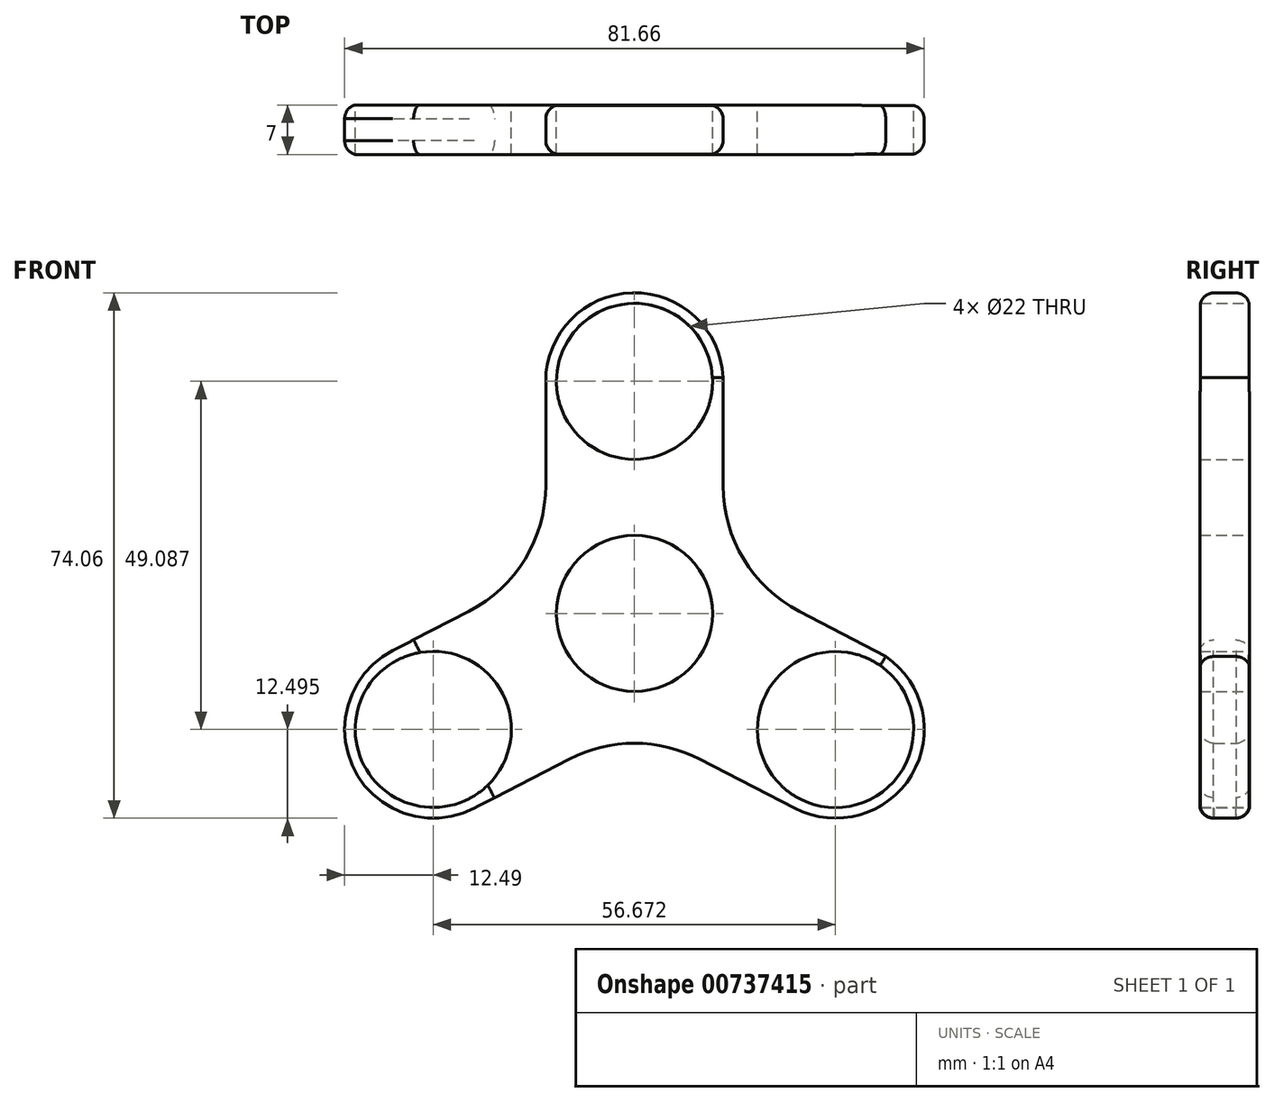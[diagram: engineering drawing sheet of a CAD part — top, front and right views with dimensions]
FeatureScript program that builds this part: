
annotation { "Feature Type Name" : "Feature", "Feature Type Description" : "" }
export const myFeature = defineFeature(function(context is Context, id is Id, definition is map)
    precondition{}
    {
        {
            var Q0;
            Q0=qCreatedBy(makeId("Front.planeOp"),FACE);
            var sketch = newSketch(context, id + "F0", { "sketchPlane" : qUnion([Q0])});
            skLineSegment(sketch, "E0", {"start": v(-27, 38.07) * mm, "end": v(-27, 0) * mm});
            skLineSegment(sketch, "E1", {"start": v(-27, 0) * mm, "end": v(-44.34, 0) * mm});
            skLineSegment(sketch, "E2", {"start": v(-44.34, 0) * mm, "end": v(-31.06, 17.05) * mm});
            skLineSegment(sketch, "E3", {"start": v(-31.06, 17.05) * mm, "end": v(-36.78, 29.22) * mm});
            skLineSegment(sketch, "E4", {"start": v(-36.78, 29.22) * mm, "end": v(-31.06, 35.49) * mm});
            skLineSegment(sketch, "E5", {"start": v(-31.06, 35.49) * mm, "end": v(-33.28, 47.29) * mm});
            skLineSegment(sketch, "E6", {"start": v(-33.28, 47.29) * mm, "end": v(-29.59, 47.29) * mm});
            skLineSegment(sketch, "E7", {"start": v(-29.59, 47.29) * mm, "end": v(-29.59, 35.49) * mm});
            skLineSegment(sketch, "E8", {"start": v(-29.59, 35.49) * mm, "end": v(-27, 35.49) * mm});
            skSolve(sketch);
        }
        {
            var Q0;
            Q0=qCreatedBy(makeId("Front.planeOp"),FACE);
            var sketch = newSketch(context, id + "F1", { "sketchPlane" : qUnion([Q0])});
            skCircle(sketch, "E9", {"center": v(0, 0) * mm, "radius": 11 * mm});
            skCircle(sketch, "E10", {"center": v(0, 32.72) * mm, "radius": 11 * mm});
            skCircle(sketch, "E11.1.0", {"center": v(-28.35, -16.35) * mm, "radius": 11 * mm});
            skCircle(sketch, "E11.2.0", {"center": v(28.32, -16.36) * mm, "radius": 11 * mm});
            skArc(sketch, "E12", {"start": v(22.58, -27.47) * mm, "mid": v(39.74, -21.45) * mm, "end": v(32.72, -4.67) * mm});
            skArc(sketch, "E13.1.0", {"start": v(12.48, 32.15) * mm, "mid": v(0.27, 45.2) * mm, "end": v(-12.5, 32.7) * mm});
            skArc(sketch, "E13.2.0", {"start": v(-34.08, -5.26) * mm, "mid": v(-39.44, -22.1) * mm, "end": v(-22.6, -27.47) * mm});
            skLineSegment(sketch, "E14", {"start": v(35.4, -6.06) * mm, "end": v(23.23, 0.29) * mm});
            skLineSegment(sketch, "E15", {"start": v(12.48, 18.02) * mm, "end": v(12.48, 33.26) * mm});
            skLineSegment(sketch, "E16", {"start": v(-12.5, 32.7) * mm, "end": v(-12.5, 18.07) * mm});
            skLineSegment(sketch, "E17", {"start": v(-23.32, 0.3) * mm, "end": v(-34.08, -5.26) * mm});
            skLineSegment(sketch, "E18", {"start": v(-22.6, -27.47) * mm, "end": v(-9.2, -20.53) * mm});
            skLineSegment(sketch, "E19", {"start": v(9.19, -20.54) * mm, "end": v(22.58, -27.47) * mm});
            skPoint(sketch, "E20.visualSharp", {"position": v(-12.5, 5.9) * mm});
            skArc(sketch, "E20.filletArc", {"start": v(-23.32, 0.3) * mm, "mid": v(-15.42, 7.67) * mm, "end": v(-12.5, 18.07) * mm});
            skPoint(sketch, "E21.visualSharp", {"position": v(0, -15.78) * mm});
            skArc(sketch, "E21.filletArc", {"start": v(9.19, -20.54) * mm, "mid": v(0, -18.3) * mm, "end": v(-9.2, -20.53) * mm});
            skPoint(sketch, "E22.visualSharp", {"position": v(12.48, 5.9) * mm});
            skArc(sketch, "E22.filletArc", {"start": v(12.48, 18.02) * mm, "mid": v(15.38, 7.65) * mm, "end": v(23.23, 0.29) * mm});
            skSolve(sketch);
        }
        {
            var Q0;
            Q0=makeQuery(id+"F1.imprint","IMPRINT",FACE,{"disambiguationData":[TD([[makeQuery(id+"F1.imprint","IMPRINT",EDGE,{"derivedFrom":sQuery(id+"F1.wireOp",EDGE,"E9")}),-1.0]])]});
            extrude(context, id + "F2", {"entities" : qUnion([Q0]), "depth" : 7 * mm, "offsetDistance" : 25 * mm});
        }
        {
            var Q0;
            Q0=makeQuery(id+"F2.opExtrude","CAP_EDGE",EDGE,{"disambiguationData":[OSD([sQuery(id+"F1.wireOp",EDGE,"E16")])],"isStart":false});
            var Q1;
            Q1=makeQuery(id+"F2.opExtrude","CAP_EDGE",EDGE,{"disambiguationData":[OSD([sQuery(id+"F1.wireOp",EDGE,"E20.filletArc")])],"isStart":false});
            var Q2;
            Q2=makeQuery(id+"F2.opExtrude","CAP_EDGE",EDGE,{"disambiguationData":[OSD([sQuery(id+"F1.wireOp",EDGE,"E17")])],"isStart":false});
            var Q3;
            Q3=makeQuery(id+"F2.opExtrude","CAP_EDGE",EDGE,{"disambiguationData":[OSD([sQuery(id+"F1.wireOp",EDGE,"E13.2.0")])],"isStart":false});
            var Q4;
            Q4=makeQuery(id+"F2.opExtrude","CAP_EDGE",EDGE,{"disambiguationData":[OSD([sQuery(id+"F1.wireOp",EDGE,"E18")])],"isStart":false});
            var Q5;
            Q5=makeQuery(id+"F2.opExtrude","CAP_EDGE",EDGE,{"disambiguationData":[OSD([sQuery(id+"F1.wireOp",EDGE,"E21.filletArc")])],"isStart":false});
            var Q6;
            Q6=makeQuery(id+"F2.opExtrude","CAP_EDGE",EDGE,{"disambiguationData":[OSD([sQuery(id+"F1.wireOp",EDGE,"E19")])],"isStart":false});
            var Q7;
            Q7=makeQuery(id+"F2.opExtrude","CAP_EDGE",EDGE,{"disambiguationData":[OSD([sQuery(id+"F1.wireOp",EDGE,"E12")])],"isStart":false});
            var Q8;
            Q8=makeQuery(id+"F2.opExtrude","CAP_EDGE",EDGE,{"disambiguationData":[OSD([sQuery(id+"F1.wireOp",EDGE,"E14")])],"isStart":false});
            var Q9;
            Q9=makeQuery(id+"F2.opExtrude","CAP_EDGE",EDGE,{"disambiguationData":[OSD([sQuery(id+"F1.wireOp",EDGE,"E22.filletArc")])],"isStart":false});
            var Q10;
            Q10=makeQuery(id+"F2.opExtrude","CAP_EDGE",EDGE,{"disambiguationData":[OSD([sQuery(id+"F1.wireOp",EDGE,"E15")])],"isStart":false});
            var Q11;
            Q11=makeQuery(id+"F2.opExtrude","CAP_EDGE",EDGE,{"disambiguationData":[OSD([sQuery(id+"F1.wireOp",EDGE,"E13.1.0")])],"isStart":false});
            var Q12;
            Q12=makeQuery(id+"F2.opExtrude","CAP_EDGE",EDGE,{"disambiguationData":[OSD([sQuery(id+"F1.wireOp",EDGE,"E15")])],"isStart":true});
            var Q13;
            Q13=makeQuery(id+"F2.opExtrude","CAP_EDGE",EDGE,{"disambiguationData":[OSD([sQuery(id+"F1.wireOp",EDGE,"E20.filletArc")])],"isStart":true});
            fillet(context, id + "F3", {"entities" : qUnion([Q0, Q1, Q2, Q3, Q4, Q5, Q6, Q7, Q8, Q9, Q10, Q11, Q12, Q13]), "radius" : 2 * mm, "tangentPropagation" : true, "allowEdgeOverflow" : false});
        }
    });
